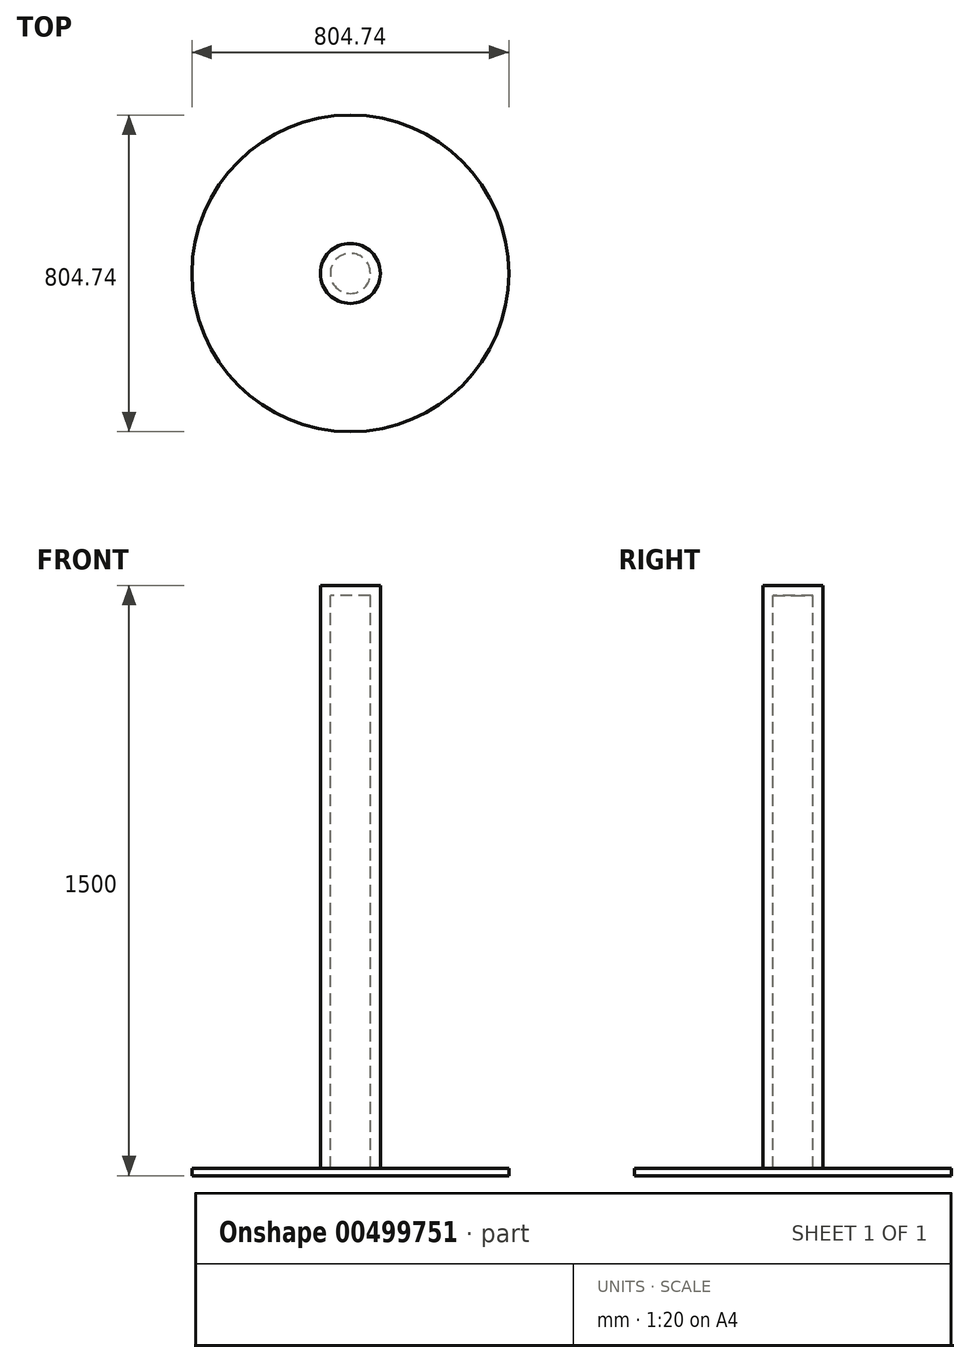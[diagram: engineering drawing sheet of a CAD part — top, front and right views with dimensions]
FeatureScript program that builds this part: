
annotation { "Feature Type Name" : "Feature", "Feature Type Description" : "" }
export const myFeature = defineFeature(function(context is Context, id is Id, definition is map)
    precondition{}
    {
        {
            var Q0;
            Q0=qCreatedBy(makeId("Right.planeOp"),FACE);
            var sketch = newSketch(context, id + "F0", { "sketchPlane" : qUnion([Q0])});
            skLineSegment(sketch, "E0", {"start": v(-402.37, 0) * mm, "end": v(-402.37, 19.05) * mm});
            skLineSegment(sketch, "E1", {"start": v(-402.37, 19.05) * mm, "end": v(-76.2, 19.05) * mm});
            skLineSegment(sketch, "E2", {"start": v(-50.8, 19.05) * mm, "end": v(0, 19.05) * mm});
            skLineSegment(sketch, "E3", {"start": v(-76.2, 1500) * mm, "end": v(-76.2, 19.05) * mm});
            skLineSegment(sketch, "E4", {"start": v(-50.8, 19.05) * mm, "end": v(-50.8, 1474.6) * mm});
            skLineSegment(sketch, "E5", {"start": v(0, 1474.6) * mm, "end": v(-50.8, 1474.6) * mm});
            skLineSegment(sketch, "E6", {"start": v(-76.2, 1500) * mm, "end": v(0, 1500) * mm});
            skLineSegment(sketch, "E7", {"start": v(-402.37, 0) * mm, "end": v(0, 0) * mm});
            skLineSegment(sketch, "E8", {"start": v(0, 1500) * mm, "end": v(0, 1474.6) * mm});
            skLineSegment(sketch, "E9", {"start": v(0, 19.05) * mm, "end": v(0, 0) * mm});
            skSolve(sketch);
        }
        {
            var Q0;
            Q0=makeQuery(id+"F0.imprint","IMPRINT",FACE,{"disambiguationData":[TD([[makeQuery(id+"F0.imprint","IMPRINT",EDGE,{"derivedFrom":sQuery(id+"F0.wireOp",EDGE,"E0")}),-1.0]])]});
            var Q1;
            Q1=sQuery(id+"F0.wireOp",EDGE,"E9");
            revolve(context, id + "F1", {"entities" : qUnion([Q0]), "axis" : qUnion([Q1]), "revolveType" : RevolveType.FULL});
        }
    });
